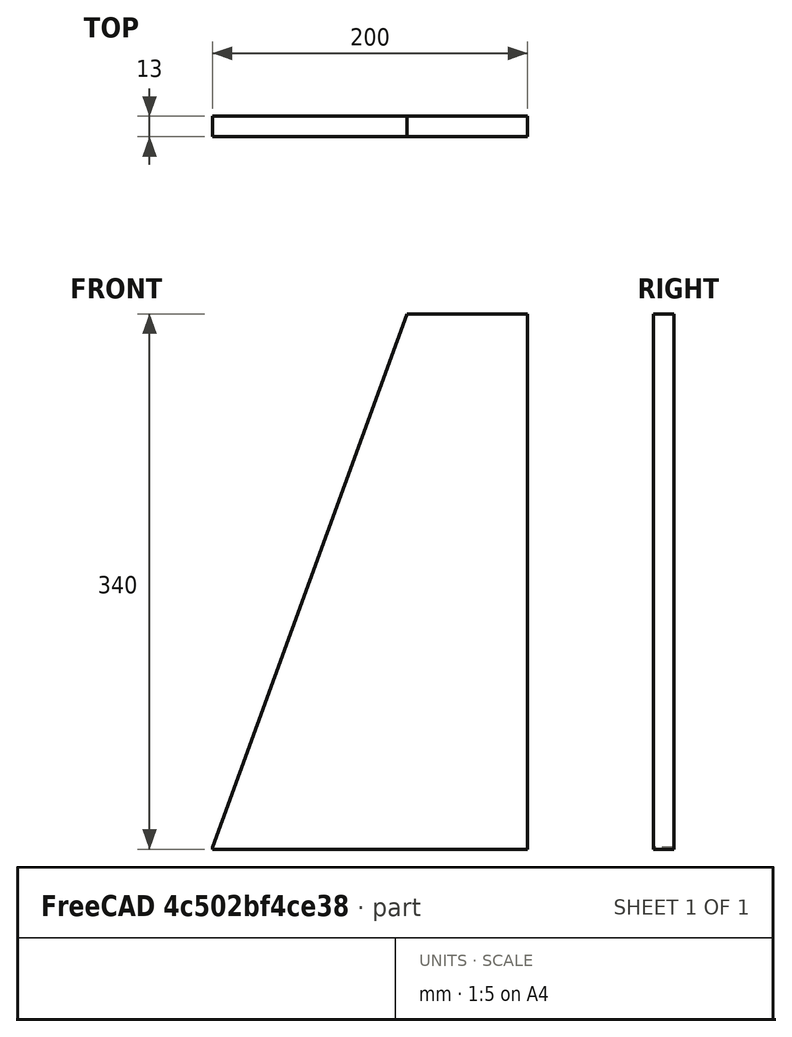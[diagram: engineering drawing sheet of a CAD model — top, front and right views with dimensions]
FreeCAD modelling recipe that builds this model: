
FCSTD DOCUMENT  (FreeCAD 0.19R24276 (Git))
Label: 8050_Frame_Side
License: All rights reserved
LicenseURL: http://en.wikipedia.org/wiki/All_rights_reserved
objects: Sketcher::SketchObject×1, PartDesign::Pad×1, PartDesign::Body×1, App::MeasureDistance×1
note: 4 computed .brp shape members not serialized (recipe doc carries the construction recipe); baked Part::Feature solids carry a one-line shape summary decoded from their .brp

FEATURE [Sketcher::SketchObject] Sketch  label="SideWall"
  FullyConstrained = true
  MapMode = 5
  Placement = pos=(0,0,0) rot=(1,0,0;1.5708rad)
  Support = -> [XZ_Plane]
  sketch-geometry (5):
    g0: LineSegment StartX=0 StartY=0 StartZ=0 EndX=200 EndY=0 EndZ=0
    g1: LineSegment StartX=200 StartY=0 StartZ=0 EndX=200 EndY=340 EndZ=0
    g2: LineSegment StartX=200 StartY=340 StartZ=0 EndX=123.386 EndY=340 EndZ=0
    g3: LineSegment StartX=123.386 StartY=340 StartZ=0 EndX=0 EndY=1 EndZ=0
    g4: LineSegment StartX=0 StartY=1 StartZ=0 EndX=0 EndY=0 EndZ=0
  constraints (14):
    c: Horizontal(g0)
    c: Vertical(g1)
    c: Coincident(g2,g1)
    c: Vertical(g4)
    c: Coincident(g2,g3)
    c: Angle(g3,g2) = 1.91986
    c: DistanceY(g4,g4) = 1
    c: Coincident(g0,g4)
    c: Perpendicular(g1,g2)
    c: DistanceY(g1,g1) = 340
    c: DistanceX(g0,g0) = 200
    c: Coincident(g3,g4)
    c: Coincident(g1,g0)
    c: Coincident(g-1,g0)
FEATURE [PartDesign::Pad] Pad
  AllowMultiFace = false
  Direction = (1,1,1)
  Length = 13
  Length2 = 100
  Midplane = true
  Placement = pos=(0,0,0) rot=(1,0,0;1.5708rad)
  Profile = -> Sketch
  Type = 0
FEATURE [PartDesign::Body] Body
  Group = -> [Sketch,Pad]
  Origin = -> Origin
  Tip = -> Pad
FEATURE [App::MeasureDistance] Distance  label="Distance: 302,70 mm"
  Distance = 302.705
  P1 = (0,-487.5,-2.51717)
  P2 = (199.669,-260,0)
